# Revit family: PRD_FrankeWS_WtrSpplFttngsFrWshBsnsAndTrghs_ElectronicThermostaticMixer_F3ET1001-1003
name_source: partatom
category: Plumbing Fixtures
revit_build: Autodesk Revit 2018 (Build: 20190510_1515(x64)
units: mm (PartAtom-declared; Revit-internal decimal feet)

## family parameters
Cut with Voids When Loaded = No
Host = Face
OmniClass Number = 23.45.55.17
OmniClass Title = Mixing Faucets
Part Type = Normal
Room Calculation Point = No
Round Connector Dimension = Use Diameter
Shared = No

## types (3) — shared parameters
AdjustableFlowTime = yes
AssetType = Fixed
Category = Pr_40_20_87_98, Washbasin taps
Color = Chrome
Default Elevation = 850 mm  [stored 2.78871 ft]
DefaultAutomaticHygieneFlushing = 24h after the last activity
DefaultFlowTime = 10.00 seconds
Depressurised = no
DiameterNominal = 15.000 mm
DurationUnit = year
FaucetFunction = MIXED
FaucetOperation = ELECTRONIC
FaucetType = BIB
Features = For sanitary facilities. For connection to hot and cold water, high-polished chromium-plated brass.
Finish = high-polished chromium-plated brass
FlowColdWater = 0.1 L/s
FlowHotWater = 0.1 L/s
FunctionalPrinciple = electronic self-closing
HygieneFlushing = yes
IfcExportAs = IfcValveType
IfcExportType = FAUCET
InletSize = G-1-2-B
Manufacturer = KWC Group AG
ManufacturerName = KWC Group AG
ManufacturerURL = www.kwc.com
Material = Brass
MaterialsBody = Brass
MaximumFlowTime = 255.00 seconds
MinimumFlowPressure = 1.00 bar
MinimumFlowTime = 1.00 seconds
NBSDescription = Water supply fittings for wash basins and troughs
NBSReference = 45-35-70/371
NominalWidth = 300 mm
OutletMaterial = PRD_AR_SyntheticGrey
PowerConsumption = 1.5
PowerSupplyConnection = Battery 6 V
ProductInformation = https://pim.kwc.com
ProtectiveShutdown = yes
ProtectiveSystemIP = IP59K
SensorMaterial = PRD_AR_SyntheticDarkGrey
SoundInsulation = no
TapBottomOffset = 72 mm  [stored 0.23622 ft]
TapMaterial = PRD_AR_ChromatedBrass_HighPolished
ThermalDisinfection = manual thermal disinfection
TypeOfMixing = with thermostat
TypeOfMounting = Wall mounting
TypeOfOperation = sensor operation
TypeOfSensor = opto-electronic sensor
TypeOfTap = bib tap
URL = www.kwc.com
Uniclass2015Code = Pr_40_20_87_98
Uniclass2015Title = Washbasin taps
Uniclass2015Version = Products v1.10
Version = 1
VolumeFlowRate = 0.10 L/s at 3 bar
WarrantyDurationUnit = year
zero-valued in all types: NominalHeight, NominalLength

## per-type parameters (varying)
| type | BIMObjectName | Description | GrossWeight | LengthToSpout | Model | ModelNumber | ModelReference | Name | NetWeight | SpoutProjection |
| F3ET1003 - 0.10 L/s with 6 V lithium battery, projection 250 mm | PRD_AR_WaterSupplyFittingsForWashBasinsAndTroughs_ElectronicThermostaticMixer_F3ET1003 | F3E-Therm thermostatic mixer DN 15 for wall mounting with lockable swivelling spout, for sanitary facilities. Opto-electronically controlled, triggered via hand movement. Thermostat with metal handle with adjustable and turn-proof temperature stop. With the option of manual thermal disinfection. For connection to hot and cold water. Control electronics, solenoid valve cartridge, 6 V lithium battery (CR-P2) and sensor in all-metal housing, high-polished chromium-plated brass. Laminar jet controller with integrated flow regulator 6.0 l/min. With adjustable connections with backflow preventer, strainers and screw rosettes. Projection 250 mm. Activated water hygiene flushing 24 hours after last activation, safety switch-off with continuous reflection and saving of statistical data. With option for parameterization and communication via optional, bidirectional remote control. | 4.25 kg | 250 mm  [stored 0.82021 ft] | F3ET1003 | 2030026612 | F3ET1003 | F3 electronic thermostatic mixer F3ET1003 | 4.00 kg | 250.00 mm |
| F3ET1002 - 0.10 L/s with 6 V lithium battery, projection 190 mm | PRD_AR_WaterSupplyFittingsForWashBasinsAndTroughs_ElectronicThermostaticMixer_F3ET1002 | F3E-Therm thermostatic mixer DN 15 for wall mounting with lockable swivelling spout, for sanitary facilities. Opto-electronically controlled, triggered via hand movement. Thermostat with metal handle with adjustable and turn-proof temperature stop. With the option of manual thermal disinfection. For connection to hot and cold water. Control electronics, solenoid valve cartridge, 6 V lithium battery (CR-P2) and sensor in all-metal housing, high-polished chromium-plated brass. Laminar jet controller with integrated flow regulator 6.0 l/min. With adjustable connections with backflow preventer, strainers and screw rosettes. Projection 190 mm. Activated water hygiene flushing 24 hours after last activation, safety switch-off with continuous reflection and saving of statistical data. With option for parameterization and communication via optional, bidirectional remote control. | 4.20 kg | 190 mm | F3ET1002 | 2030032506 | F3ET1002 | F3 electronic thermostatic mixer F3ET1002 | 3.90 kg | 190.00 mm |
| F3ET1001 - 0.10 L/s with 6 V lithium battery, projection 130 mm | PRD_AR_WaterSupplyFittingsForWashBasinsAndTroughs_ElectronicThermostaticMixer_F3ET1001 | F3E-Therm thermostatic mixer DN 15 for wall mounting with lockable swivelling spout, for sanitary facilities. Opto-electronically controlled, triggered via hand movement. Thermostat with metal handle with adjustable and turn-proof temperature stop. With the option of manual thermal disinfection. For connection to hot and cold water. Control electronics, solenoid valve cartridge, 6 V lithium battery (CR-P2) and sensor in all-metal housing, high-polished chromium-plated brass. Laminar jet controller with integrated flow regulator 6.0 l/min. With adjustable connections with backflow preventer, strainers and screw rosettes. Projection 130 mm. Activated water hygiene flushing 24 hours after last activation, safety switch-off with continuous reflection and saving of statistical data. With option for parameterization and communication via optional, bidirectional remote control. | 4.10 kg | 130 mm  [stored 0.426509 ft] | F3ET1001 | 2030032507 | F3ET1001 | F3 electronic thermostatic mixer F3ET1001 | 3.85 kg | 130.00 mm |

note: [stored X ft] marks values corroborated as IEEE doubles in the binary element streams (Revit-internal decimal feet)

## geometry (parser evidence)
native form markers: Sweep x3
no freeform markers — native parametric forms only
